# Revit family: Medical_All_Liko-Overhead_Lift_System_Traverse-Ceiling-Mounted
name_source: partatom
category: Specialty Equipment
revit_build: Autodesk Revit Architecture 2015 (Build: 20140606_1530(x64)
units: mm (PartAtom-declared; Revit-internal decimal feet)

## types (1)
- Traverse Ceiling Mounted Lift
    Amperage = 12 A
    Apparent Load = 0 VA
    BIMobject category = All
    BIMobject category code = medical-all
    BIMobject main category = Medical
    BIMobject main category code = medical
    Batteries = Lithium-ion 25.5V/4.2Ah
    Brand url = https://construction.hill-rom.com
    Default Elevation = 4' - 0"
    Description = Ceiling Mounted
    Design country = United States
    Edition number = 1
    Electrical Connector Description = Electrical Connector Description
    Emergency Lowering = Manual&Electrical
    Emergency Raising = Electrical
    Finish = Stainless Steel-Hill-Rom-Silver
    Frequency = 0 Hz
    Hand Control Safety Class = IP X7
    Installation instructions = https://construction.hill-rom.com
    Length = 8' - 0"
    Lift Motor = Overhead_Lift-Liko-Pendant : Pendant Adjustable 500-900mm
    Lift Motor Safety Class = IP X4
    Lift Offset from Left = 4' - 0"
    Manufacturer = Liko
    Manufacturer country = United States
    Manufacturer name = Hill-Rom
    Masterformat 2014 Code = 11 25 00
    Masterformat 2014 Description = Hospitality Equipment
    Maximum Overhang = 1' - 6"
    Maximum Pendants = 3
    Model = Traverse Ceiling Mounted Lift
    Nominal height = 0' - 0"
    Nominal width = 0' - 0"
    Number of Pendants = 3
    OmniClass Code = 23-25 49 13
    OmniClass Description = Patient lifts
    Pendant = Overhead_Lift-Liko-Pendant : Pendant Adjustable 500-900mm
    Pendant Height = 2' - 0"
    Power Factor = 1
    Power Source = Built in battery pack
    Primary Rail = Overhead_Lift-Liko-Pendant : Pendant Adjustable 500-900mm
    Product Guid = 82cc0e31-91a0-4ff4-87d7-64fa409ed2a9
    Product SKU = Liko-Overhead-Lift-Traverse-Rail
    Product data url = https://bimobject.com
    Product family = Overhead Patient Lift System
    Product group = Non-Bariatric
    Product url = https://www.hill-rom.com
    QR code = http://bimobject.com
    Secondary Rail = Overhead_Lift-Liko-Pendant : Pendant Adjustable 500-900mm
    Secondary Rail Overhang = 0' - 6"
    Technical description = https://construction.hill-rom.com
    Traverse Rail Carrier = Overhead_Lift-Liko-Pendant : Pendant Adjustable 500-900mm
    Traverse Rail Offset from Left = 4' - 0"
    URL = http://www.liko.se
    Universal Singbar 600 = No
    Voltage = 24 V
    Weight Net (Kg) = 0
    Width = 8' - 0"
    Youtube clip = https://www.hill-rom.ca

## geometry (parser evidence)
native form markers: Blend x2, Sweep x9
no freeform markers — native parametric forms only
